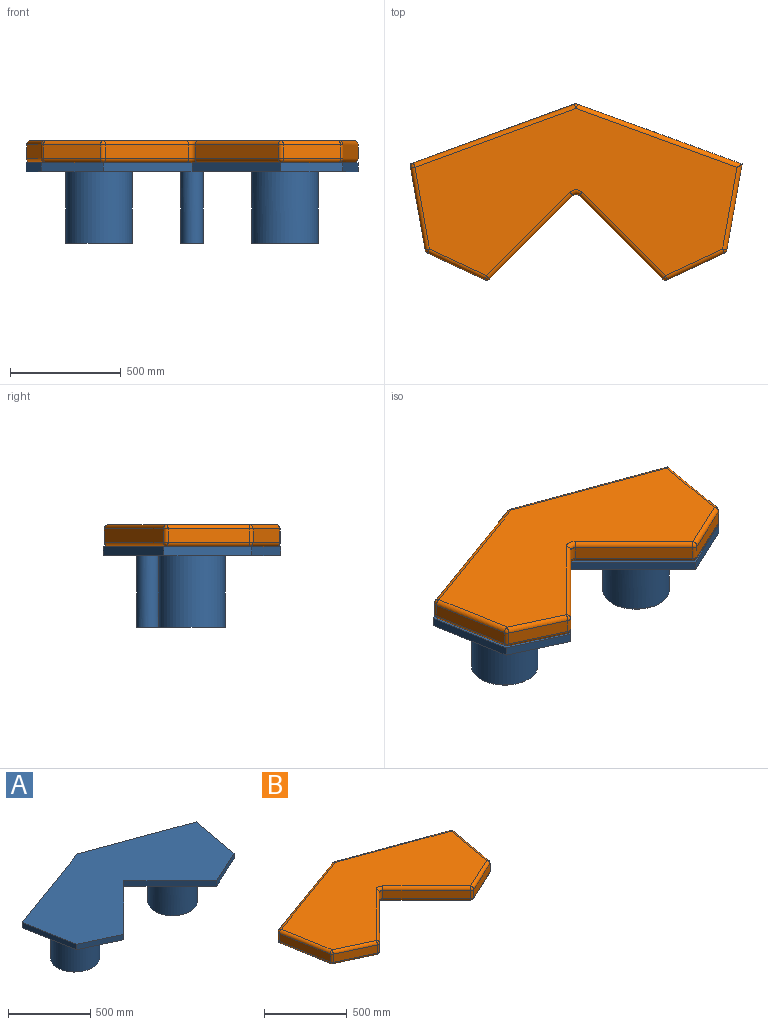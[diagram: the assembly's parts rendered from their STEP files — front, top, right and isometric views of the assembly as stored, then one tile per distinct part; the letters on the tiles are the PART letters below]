
ASSEMBLY  parts=2 mates=1
PART A: 22 faces, bbox 1500x800x365 mm
  f0: plane 280.1x130.61mm, normal (-0.42,-0.91,0), area 12362.4mm2, adj f1,f7,f8,f9
  f1: plane 400x400mm, normal (0.71,-0.71,0), area 22627.4mm2, adj f0,f2,f8,f9
  f2: plane 400x400mm, normal (-0.71,-0.71,0), area 22627.4mm2, adj f1,f3,f8,f9
  f3: plane 280.1x130.61mm, normal (0.42,-0.91,0), area 12362.4mm2, adj f2,f4,f8,f9
  f4: plane 396.41x69.9mm, normal (0.98,-0.17,0), area 16100.9mm2, adj f3,f5,f8,f9
  f5: plane 750x272.98mm, normal (0.34,0.94,0), area 31925.3mm2, adj f4,f6,f8,f9
  f6: plane 750x272.98mm, normal (-0.34,0.94,0), area 31925.3mm2, adj f5,f7,f8,f9
  f7: plane 396.41x69.9mm, normal (-0.98,-0.17,0), area 16100.9mm2, adj f0,f6,f8,f9
  f8: plane 1500x800mm, normal (0,0,1), area 752714.3mm2, adj f0,f1,f2,f3,f4,f5,f6,f7
  f9: plane 1500x800mm, normal (0,0,-1), area 603488.7mm2, adj f0,f1,f2,f3,f4,f5,f6,f7
  f10: cylinder r=147mm len=325mm, axis (0,0,1), area 300179.2mm2, adj f12,f13
  f11: cylinder r=150mm len=325mm, axis (0,0,1), area 306305.3mm2, adj f9,f12
  f12: plane 300x300mm, normal (0,0,-1), area 2799.2mm2, adj f10,f11
  f13: plane 294x294mm, normal (0,0,-1), area 67886.7mm2, adj f10
  f14: cylinder r=147mm len=325mm, axis (0,0,1), area 300179.2mm2, adj f16,f17
  f15: cylinder r=150mm len=325mm, axis (0,0,1), area 306305.3mm2, adj f9,f16
  f16: plane 300x300mm, normal (0,0,-1), area 2799.2mm2, adj f14,f15
  f17: plane 294x294mm, normal (0,0,-1), area 67886.7mm2, adj f14
  f18: cylinder r=48mm len=325mm, axis (0,0,1), area 98017.7mm2, adj f20,f21
  f19: cylinder r=50mm len=325mm, axis (0,0,1), area 102101.8mm2, adj f9,f20
  f20: plane 100x100mm, normal (0,0,-1), area 615.8mm2, adj f18,f19
  f21: plane 96x96mm, normal (0,0,-1), area 7238.2mm2, adj f18
PART B: 47 faces, bbox 1497.4x794.7x100 mm
  f0: plane 257.97x120.3mm, normal (-0.42,-0.91,0), area 17078.6mm2, adj f20,f21,f30,f31
  f1: plane 375.96x375.96mm, normal (0.71,-0.71,0), area 31900.9mm2, adj f29,f30,f40,f41
  f2: plane 375.96x375.96mm, normal (-0.71,-0.71,0), area 31900.9mm2, adj f35,f40,f43,f46
  f3: plane 257.97x120.3mm, normal (0.42,-0.91,0), area 17078.6mm2, adj f33,f34,f42,f43
  f4: plane 386.16x68.09mm, normal (0.98,-0.17,0), area 23526.7mm2, adj f5,f24,f32,f33
  f5: plane 743.16x270.49mm, normal (0.34,0.94,0), area 47451.2mm2, adj f4,f18,f19,f27
  f6: plane 727.39x264.75mm, normal (-0.34,0.94,0), area 46444.3mm2, adj f11,f13,f17,f18
  f7: plane 369.63x65.18mm, normal (-0.98,-0.17,0), area 22519.8mm2, adj f12,f13,f21,f22
  f8: plane 1454.78x754.67mm, normal (0,0,1), area 671435.1mm2, adj f17,f22,f27,f31,f32,f41,f42,f44
  f9: plane 1454.78x754.67mm, normal (0,0,-1), area 671435.1mm2, adj f11,f12,f19,f20,f24,f29,f34,f35
  f10: sphere r=20mm, area 558.5mm2, adj f11,f12,f13
  f11: cylinder r=20mm len=734.23mm, axis (-0.94,-0.34,0), area 24318.2mm2, adj f6,f9,f10,f14
  f12: cylinder r=20mm len=373.1mm, axis (0.17,-0.98,0), area 11791.3mm2, adj f7,f9,f10,f15
  f13: cylinder r=20mm len=60mm, axis (0,0,-1), area 1675.5mm2, adj f6,f7,f10,f16
  f14: sphere r=20mm, area 279.3mm2, adj f11,f18,f19
  f15: sphere r=20mm, area 384mm2, adj f12,f20,f21
  f16: sphere r=20mm, area 558.5mm2, adj f13,f17,f22
  f17: cylinder r=20mm len=734.23mm, axis (0.94,0.34,0), area 24318.2mm2, adj f6,f8,f16,f23
  f18: cylinder r=20mm len=60mm, axis (0,0,1), area 837.8mm2, adj f5,f6,f14,f23
  f19: cylinder r=20mm len=750mm, axis (-0.94,0.34,0), area 24653.8mm2, adj f5,f9,f14,f24
  f20: cylinder r=20mm len=266.43mm, axis (0.91,-0.42,0), area 8942.3mm2, adj f0,f9,f15,f25
  f21: cylinder r=20mm len=60mm, axis (0,0,1), area 1151.9mm2, adj f0,f7,f15,f26
  f22: cylinder r=20mm len=373.1mm, axis (-0.17,0.98,0), area 11791.3mm2, adj f7,f8,f16,f26
  f23: sphere r=20mm, area 279.3mm2, adj f17,f18,f27
  f24: cylinder r=20mm len=389.63mm, axis (0.17,0.98,0), area 12127mm2, adj f4,f9,f19,f28
  f25: sphere r=20mm, area 488.7mm2, adj f20,f29,f30
  f26: sphere r=20mm, area 384mm2, adj f21,f22,f31
  f27: cylinder r=20mm len=750mm, axis (0.94,-0.34,0), area 24653.8mm2, adj f5,f8,f23,f32
  f28: sphere r=20mm, area 384mm2, adj f24,f33,f34
  f29: cylinder r=20mm len=390.1mm, axis (0.71,0.71,0), area 16703.3mm2, adj f1,f9,f25,f36
  f30: cylinder r=20mm len=60mm, axis (0,0,-1), area 1466.1mm2, adj f0,f1,f25,f37
  f31: cylinder r=20mm len=266.43mm, axis (-0.91,0.42,0), area 8942.3mm2, adj f0,f8,f26,f37
  f32: cylinder r=20mm len=389.63mm, axis (-0.17,-0.98,0), area 12127mm2, adj f4,f8,f27,f38
  f33: cylinder r=20mm len=60mm, axis (0,0,1), area 1151.9mm2, adj f3,f4,f28,f38
  f34: cylinder r=20mm len=266.43mm, axis (0.91,0.42,0), area 8942.3mm2, adj f3,f9,f28,f39
  f35: cylinder r=20mm len=390.1mm, axis (0.71,-0.71,0), area 16703.3mm2, adj f2,f9,f36,f39
  f36: torus R=40mm, axis (0,0,1), area 1345.6mm2, adj f9,f29,f35,f40
  f37: sphere r=20mm, area 488.7mm2, adj f30,f31,f41
  f38: sphere r=20mm, area 384mm2, adj f32,f33,f42
  f39: sphere r=20mm, area 488.7mm2, adj f34,f35,f43
  f40: cylinder r=20mm len=60mm, axis (0,0,-1), area 1885mm2, adj f1,f2,f36,f44
  f41: cylinder r=20mm len=390.1mm, axis (-0.71,-0.71,0), area 16703.3mm2, adj f1,f8,f37,f44
  f42: cylinder r=20mm len=266.43mm, axis (-0.91,-0.42,0), area 8942.3mm2, adj f3,f8,f38,f45
  f43: cylinder r=20mm len=60mm, axis (0,0,-1), area 1466.1mm2, adj f2,f3,f39,f45
  f44: torus R=40mm, axis (0,0,1), area 1345.6mm2, adj f8,f40,f41,f46
  f45: sphere r=20mm, area 488.7mm2, adj f42,f43,f46
  f46: cylinder r=20mm len=390.1mm, axis (-0.71,0.71,0), area 16703.3mm2, adj f2,f8,f44,f45
PLACE A t=(-177.92,-94.77,-124.43)mm fixed
PLACE B t=(-177.92,-96.95,-84.43)mm
MATE planar B.f9 <-> A.f8  axis (0,0,-1) through (-177.92,-91.64,-84.43)mm
